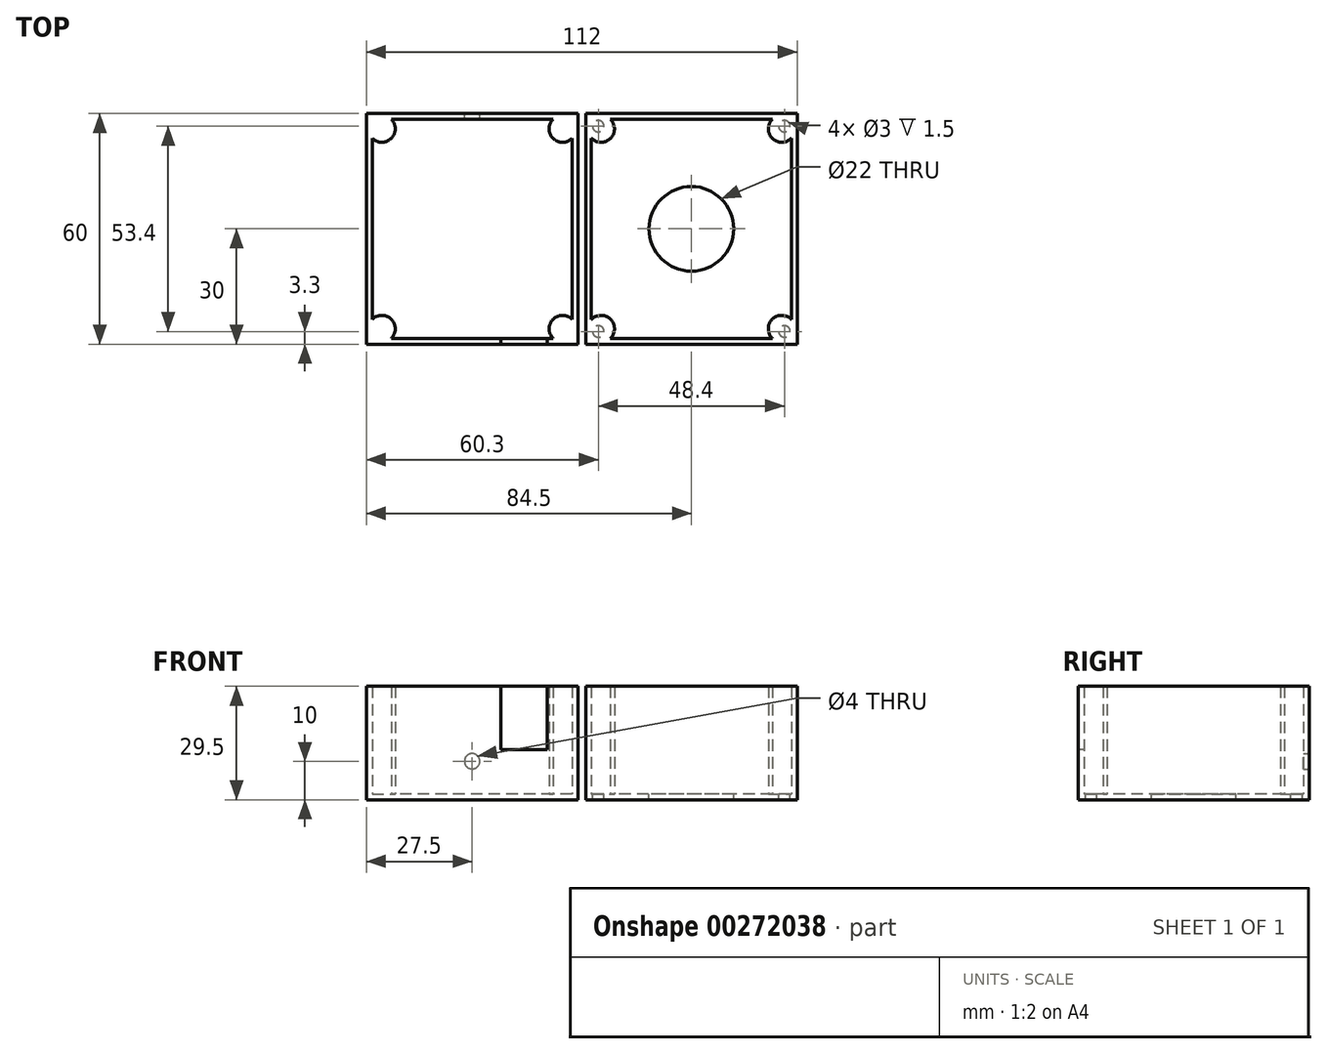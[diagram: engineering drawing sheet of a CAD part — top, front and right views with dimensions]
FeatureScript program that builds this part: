
annotation { "Feature Type Name" : "Feature", "Feature Type Description" : "" }
export const myFeature = defineFeature(function(context is Context, id is Id, definition is map)
    precondition{}
    {
        {
            var Q0;
            Q0=qCreatedBy(makeId("Top.planeOp"),FACE);
            var sketch = newSketch(context, id + "F0", { "sketchPlane" : qUnion([Q0])});
            skLineSegment(sketch, "E0.bottom", {"start": v(-56, 30) * mm, "end": v(-1, 30) * mm});
            skLineSegment(sketch, "E0.top", {"start": v(-56, -30) * mm, "end": v(-1, -30) * mm});
            skLineSegment(sketch, "E0.left", {"start": v(-56, 30) * mm, "end": v(-56, -30) * mm});
            skLineSegment(sketch, "E0.right", {"start": v(-1, 30) * mm, "end": v(-1, -30) * mm});
            skPoint(sketch, "E0.middle", {"position": v(-28.5, 0) * mm});
            skLineSegment(sketch, "E1", {"start": v(0, 30) * mm, "end": v(0, -30) * mm, "construction": true});
            skSolve(sketch);
        }
        {
            var Q0;
            Q0 = qSketchRegion(id + "F0", true);
            extrude(context, id + "F1", {"entities" : qUnion([Q0]), "depth" : 1.5 * mm});
        }
        {
            var Q0;
            Q0=makeQuery(id+"F1.opExtrude","CAP_FACE",FACE,{"disambiguationData":[OSD([sQuery(id+"F0.wireOp",EDGE,"E0.bottom"),sQuery(id+"F0.wireOp",EDGE,"E0.top"),sQuery(id+"F0.wireOp",EDGE,"E0.left"),sQuery(id+"F0.wireOp",EDGE,"E0.right")])],"isStart":false});
            var sketch = newSketch(context, id + "F2", { "sketchPlane" : qUnion([Q0])});
            skLineSegment(sketch, "E2.0", {"start": v(-54.5, 28.5) * mm, "end": v(-54.5, -28.5) * mm});
            skLineSegment(sketch, "E2.1", {"start": v(-2.5, 28.5) * mm, "end": v(-54.5, 28.5) * mm});
            skLineSegment(sketch, "E2.2", {"start": v(-2.5, -28.5) * mm, "end": v(-2.5, 28.5) * mm});
            skLineSegment(sketch, "E2.3", {"start": v(-54.5, -28.5) * mm, "end": v(-2.5, -28.5) * mm});
            skLineSegment(sketch, "E3.0.0", {"start": v(-56, 30) * mm, "end": v(-56, -30) * mm});
            skLineSegment(sketch, "E3.0.1", {"start": v(-56, -30) * mm, "end": v(-1, -30) * mm});
            skLineSegment(sketch, "E3.0.2", {"start": v(-1, -30) * mm, "end": v(-1, 30) * mm});
            skLineSegment(sketch, "E3.0.3", {"start": v(-1, 30) * mm, "end": v(-56, 30) * mm});
            skSolve(sketch);
        }
        {
            var Q0;
            Q0 = qSketchRegion(id + "F2", true);
            extrude(context, id + "F3", {"entities" : qUnion([Q0]), "operationType" : NewBodyOperationType.ADD, "depth" : 28 * mm});
        }
        {
            var Q0;
            Q0=makeQuery(id+"F1.opExtrude","CAP_FACE",FACE,{"disambiguationData":[OSD([sQuery(id+"F0.wireOp",EDGE,"E0.bottom"),sQuery(id+"F0.wireOp",EDGE,"E0.top"),sQuery(id+"F0.wireOp",EDGE,"E0.left"),sQuery(id+"F0.wireOp",EDGE,"E0.right")])],"isStart":false});
            var sketch = newSketch(context, id + "F4", { "sketchPlane" : qUnion([Q0])});
            skCircle(sketch, "E4", {"center": v(-52, 26) * mm, "radius": 2.5 * mm});
            skLineSegment(sketch, "E5", {"start": v(-28.5, 28.5) * mm, "end": v(-28.5, -28.5) * mm, "construction": true});
            skLineSegment(sketch, "E6", {"start": v(-54.5, 0) * mm, "end": v(-2.5, 0) * mm, "construction": true});
            skLineSegment(sketch, "E7.0", {"start": v(-54.5, 28.5) * mm, "end": v(-54.5, 23.55) * mm});
            skLineSegment(sketch, "E8.trimOffspring", {"start": v(-49.55, 28.5) * mm, "end": v(-54.5, 28.5) * mm});
            skCircle(sketch, "E9.MirrorC", {"center": v(-5, 26) * mm, "radius": 2.5 * mm});
            skLineSegment(sketch, "E10.MirrorCS", {"start": v(-7.45, 28.5) * mm, "end": v(-2.5, 28.5) * mm});
            skLineSegment(sketch, "E11.MirrorCS", {"start": v(-2.5, 28.5) * mm, "end": v(-2.5, 23.55) * mm});
            skLineSegment(sketch, "E12.MirrorCS", {"start": v(-49.55, -28.5) * mm, "end": v(-54.5, -28.5) * mm});
            skCircle(sketch, "E13.MirrorC", {"center": v(-52, -26) * mm, "radius": 2.5 * mm});
            skLineSegment(sketch, "E14.MirrorCS", {"start": v(-54.5, -28.5) * mm, "end": v(-54.5, -23.55) * mm});
            skLineSegment(sketch, "E15.MirrorCS", {"start": v(-7.45, -28.5) * mm, "end": v(-2.5, -28.5) * mm});
            skLineSegment(sketch, "E16.MirrorCS", {"start": v(-2.5, -28.5) * mm, "end": v(-2.5, -23.55) * mm});
            skCircle(sketch, "E17.MirrorC", {"center": v(-5, -26) * mm, "radius": 2.5 * mm});
            skLineSegment(sketch, "E18", {"start": v(-54.5, 28.5) * mm, "end": v(-52, 26) * mm, "construction": true});
            skArc(sketch, "E19.0", {"start": v(-54.45, 28.5) * mm, "mid": v(-54.47, 28.47) * mm, "end": v(-54.5, 28.45) * mm});
            skArc(sketch, "E20.trimOffspring", {"start": v(-54.5, 23.55) * mm, "mid": v(-49.53, 23.53) * mm, "end": v(-49.55, 28.5) * mm});
            skArc(sketch, "E21.MirrorCS", {"start": v(-2.5, 23.55) * mm, "mid": v(-7.47, 23.53) * mm, "end": v(-7.45, 28.5) * mm});
            skArc(sketch, "E22.MirrorCS", {"start": v(-54.5, -23.55) * mm, "mid": v(-49.53, -23.53) * mm, "end": v(-49.55, -28.5) * mm});
            skArc(sketch, "E23.MirrorCS", {"start": v(-2.5, -23.55) * mm, "mid": v(-7.47, -23.53) * mm, "end": v(-7.45, -28.5) * mm});
            skLineSegment(sketch, "E24", {"start": v(-54.45, 28.5) * mm, "end": v(-28.5, 28.5) * mm, "construction": true});
            skSolve(sketch);
        }
        {
            var Q0;
            Q0 = qSketchRegion(id + "F4", true);
            var Q1;
            Q1=makeQuery(id+"F3.opExtrude","CAP_VERTEX",VERTEX,{"disambiguationData":[OSD([sQuery(id+"F2.wireOp",EDGE,"E2.0"),sQuery(id+"F2.wireOp",EDGE,"E2.1")])],"isStart":false});
            extrude(context, id + "F5", {"entities" : qUnion([Q0]), "operationType" : NewBodyOperationType.ADD, "endBound" : BoundingType.UP_TO_VERTEX, "endBoundEntityVertex" : qUnion([Q1]), "depth" : 25 * mm});
        }
        {
            var Q0;
            Q0=makeQuery(id+"F1.opExtrude","SWEPT_BODY",BODY,{"disambiguationData":[OSD([sQuery(id+"F0.wireOp",EDGE,"E0.bottom"),sQuery(id+"F0.wireOp",EDGE,"E0.top"),sQuery(id+"F0.wireOp",EDGE,"E0.left"),sQuery(id+"F0.wireOp",EDGE,"E0.right")])]});
            var Q1;
            Q1=qCreatedBy(makeId("Right.planeOp"),FACE);
            mirror(context, id + "F6", {"entities" : qUnion([Q0]), "mirrorPlane" : qUnion([Q1])});
        }
        {
            var Q0;
            Q0=makeQuery(id+"F6.opPattern","COPY",FACE,{"derivedFrom":makeQuery(id+"F5.boolean.opBoolean","SPLIT",FACE,{"disambiguationData":[TD([makeQuery(id+"F3.opExtrude","SWEPT_FACE",FACE,{"disambiguationData":[OSD([sQuery(id+"F2.wireOp",EDGE,"E2.0")])]})])],"derivedFrom":makeQuery(id+"F1.opExtrude","CAP_FACE",FACE,{"disambiguationData":[OSD([sQuery(id+"F0.wireOp",EDGE,"E0.bottom"),sQuery(id+"F0.wireOp",EDGE,"E0.top"),sQuery(id+"F0.wireOp",EDGE,"E0.left"),sQuery(id+"F0.wireOp",EDGE,"E0.right")])],"isStart":false})}),"instanceName":"1"});
            var sketch = newSketch(context, id + "F7", { "sketchPlane" : qUnion([Q0])});
            skCircle(sketch, "E25", {"center": v(28.5, 0) * mm, "radius": 11 * mm});
            skPoint(sketch, "E25.centerSnap0", {"position": v(28.5, 28.5) * mm});
            skCircle(sketch, "E26.0", {"center": v(4.3, 26.7) * mm, "radius": 1.5 * mm});
            skCircle(sketch, "E27.0", {"center": v(52.7, 26.7) * mm, "radius": 1.5 * mm});
            skCircle(sketch, "E28.0", {"center": v(52.7, -26.7) * mm, "radius": 1.5 * mm});
            skCircle(sketch, "E29.0", {"center": v(4.3, -26.7) * mm, "radius": 1.5 * mm});
            skSolve(sketch);
        }
        {
            var Q0;
            Q0 = qSketchRegion(id + "F7", true);
            extrude(context, id + "F8", {"entities" : qUnion([Q0]), "operationType" : NewBodyOperationType.REMOVE, "endBound" : BoundingType.THROUGH_ALL, "oppositeDirection" : true, "depth" : 25 * mm});
        }
        {
            var Q0;
            Q0=makeQuery(id+"F3.boolean.opBoolean","MERGE",FACE,{"derivedFrom":[makeQuery(id+"F1.opExtrude","SWEPT_FACE",FACE,{"disambiguationData":[OSD([sQuery(id+"F0.wireOp",EDGE,"E0.top")])]}),makeQuery(id+"F3.opExtrude","SWEPT_FACE",FACE,{"disambiguationData":[OSD([sQuery(id+"F2.wireOp",EDGE,"E3.0.1")])]})]});
            var sketch = newSketch(context, id + "F9", { "sketchPlane" : qUnion([Q0])});
            skLineSegment(sketch, "E30.bottom", {"start": v(-9, 29.5) * mm, "end": v(-21, 29.5) * mm});
            skLineSegment(sketch, "E30.top", {"start": v(-9, 13) * mm, "end": v(-21, 13) * mm});
            skLineSegment(sketch, "E30.left", {"start": v(-9, 29.5) * mm, "end": v(-9, 13) * mm});
            skLineSegment(sketch, "E30.right", {"start": v(-21, 29.5) * mm, "end": v(-21, 13) * mm});
            skSolve(sketch);
        }
        {
            var Q0;
            Q0 = qSketchRegion(id + "F9", true);
            extrude(context, id + "F10", {"entities" : qUnion([Q0]), "operationType" : NewBodyOperationType.REMOVE, "endBound" : BoundingType.UP_TO_NEXT, "oppositeDirection" : true, "depth" : 25 * mm});
        }
        {
            var Q0;
            Q0=makeQuery(id+"F3.boolean.opBoolean","MERGE",FACE,{"derivedFrom":[makeQuery(id+"F1.opExtrude","SWEPT_FACE",FACE,{"disambiguationData":[OSD([sQuery(id+"F0.wireOp",EDGE,"E0.bottom")])]}),makeQuery(id+"F3.opExtrude","SWEPT_FACE",FACE,{"disambiguationData":[OSD([sQuery(id+"F2.wireOp",EDGE,"E3.0.3")])]})]});
            var sketch = newSketch(context, id + "F11", { "sketchPlane" : qUnion([Q0])});
            skLineSegment(sketch, "E31", {"start": v(28.5, 0) * mm, "end": v(28.5, 29.5) * mm, "construction": true});
            skCircle(sketch, "E32", {"center": v(28.5, 10) * mm, "radius": 2 * mm});
            skSolve(sketch);
        }
        {
            var Q0;
            Q0 = qSketchRegion(id + "F11", true);
            extrude(context, id + "F12", {"entities" : qUnion([Q0]), "operationType" : NewBodyOperationType.REMOVE, "endBound" : BoundingType.UP_TO_NEXT, "oppositeDirection" : true, "depth" : 25 * mm});
        }
    });
